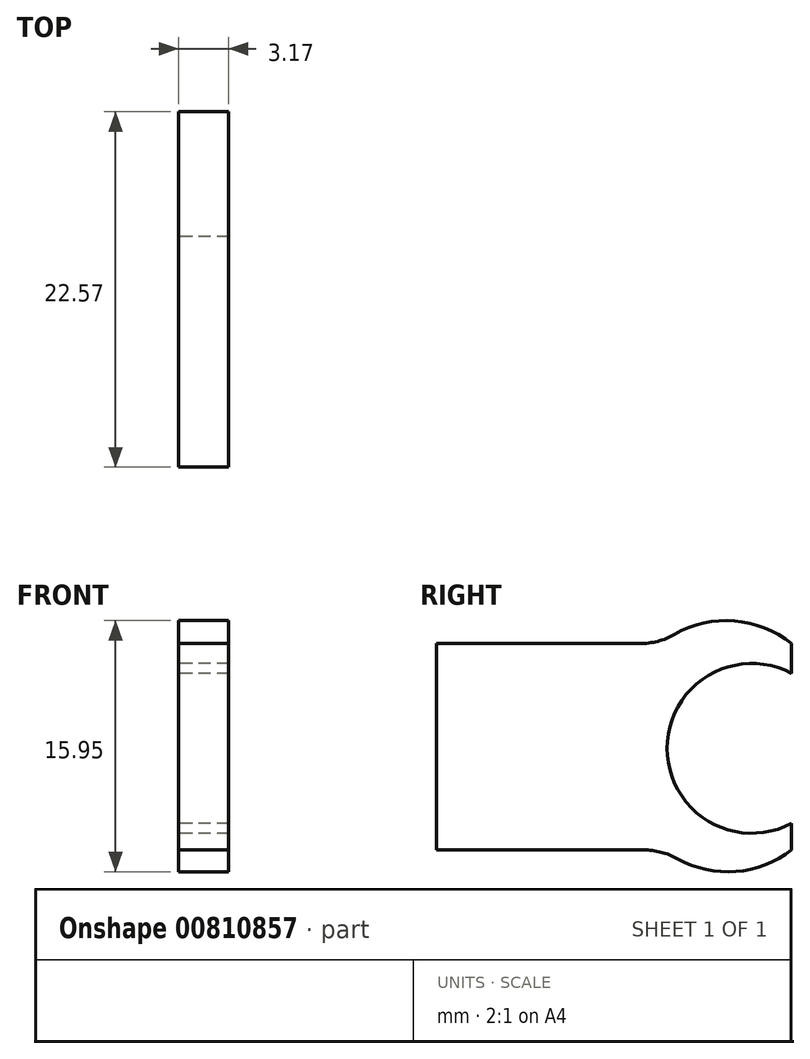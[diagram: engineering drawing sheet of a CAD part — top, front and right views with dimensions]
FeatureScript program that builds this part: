
annotation { "Feature Type Name" : "Feature", "Feature Type Description" : "" }
export const myFeature = defineFeature(function(context is Context, id is Id, definition is map)
    precondition{}
    {
        {
            var Q0;
            Q0=qCreatedBy(makeId("Right.planeOp"),FACE);
            var sketch = newSketch(context, id + "F0", { "sketchPlane" : qUnion([Q0])});
            skLineSegment(sketch, "E0.left", {"start": v(-12.97, -6.1) * mm, "end": v(-12.97, -6.1) * mm});
            skLineSegment(sketch, "E1.right", {"start": v(-12.97, 7) * mm, "end": v(-12.97, -6.1) * mm});
            skLineSegment(sketch, "E2.bottom", {"start": v(-12.97, 7) * mm, "end": v(-0.03, 7) * mm});
            skLineSegment(sketch, "E2.top", {"start": v(-12.97, -6.1) * mm, "end": v(0.2, -6.1) * mm});
            skLineSegment(sketch, "E2.right", {"start": v(9.6, 7) * mm, "end": v(9.6, -6.1) * mm});
            skArc(sketch, "E3", {"start": v(9.6, 5.12) * mm, "mid": v(1.69, 0.36) * mm, "end": v(9.6, -4.4) * mm});
            skLineSegment(sketch, "E4.left", {"start": v(-12.97, -6.1) * mm, "end": v(-12.97, 7) * mm});
            skArc(sketch, "E5", {"start": v(9.6, 7) * mm, "mid": v(5.97, 8.45) * mm, "end": v(2.17, 7.6) * mm});
            skArc(sketch, "E6", {"start": v(2.34, -6.65) * mm, "mid": v(6.06, -7.46) * mm, "end": v(9.6, -6.1) * mm});
            skPoint(sketch, "E7.newPointA", {"position": v(1.23, 6.95) * mm});
            skPoint(sketch, "E7.newPointB", {"position": v(9.6, 7) * mm});
            skArc(sketch, "E7.filletArc", {"start": v(-0.03, 7) * mm, "mid": v(1.1, 7.16) * mm, "end": v(2.17, 7.6) * mm});
            skPoint(sketch, "E8.newPointA", {"position": v(1.23, -5.88) * mm});
            skPoint(sketch, "E8.newPointB", {"position": v(9.6, -6.1) * mm});
            skArc(sketch, "E8.filletArc", {"start": v(2.34, -6.65) * mm, "mid": v(1.3, -6.24) * mm, "end": v(0.2, -6.1) * mm});
            skSolve(sketch);
        }
        {
            var Q0;
            {var subQ3=sQuery(id+"F0.wireOp",EDGE,"I5QzVo2a-R8Gp-gC0j-RGT5-BMx39ckJmGD2.bottom");Q0=makeQuery(id+"F0.imprint","IMPRINT",FACE,{"disambiguationData":[TD([[makeQuery(id+"F0.imprint","IMPRINT",EDGE,{"derivedFrom":subQ3}),1.0]])]});}
            var Q1;
            Q1=makeQuery(id+"F0.imprint","IMPRINT",FACE,{"disambiguationData":[TD([[makeQuery(id+"F0.imprint","IMPRINT",EDGE,{"derivedFrom":sQuery(id+"F0.wireOp",EDGE,"E2.bottom")}),-1.0]])]});
            extrude(context, id + "F1", {"entities" : qUnion([Q0, Q1]), "depth" : 3.17 * mm, "offsetDistance" : 25.4 * mm});
        }
    });
